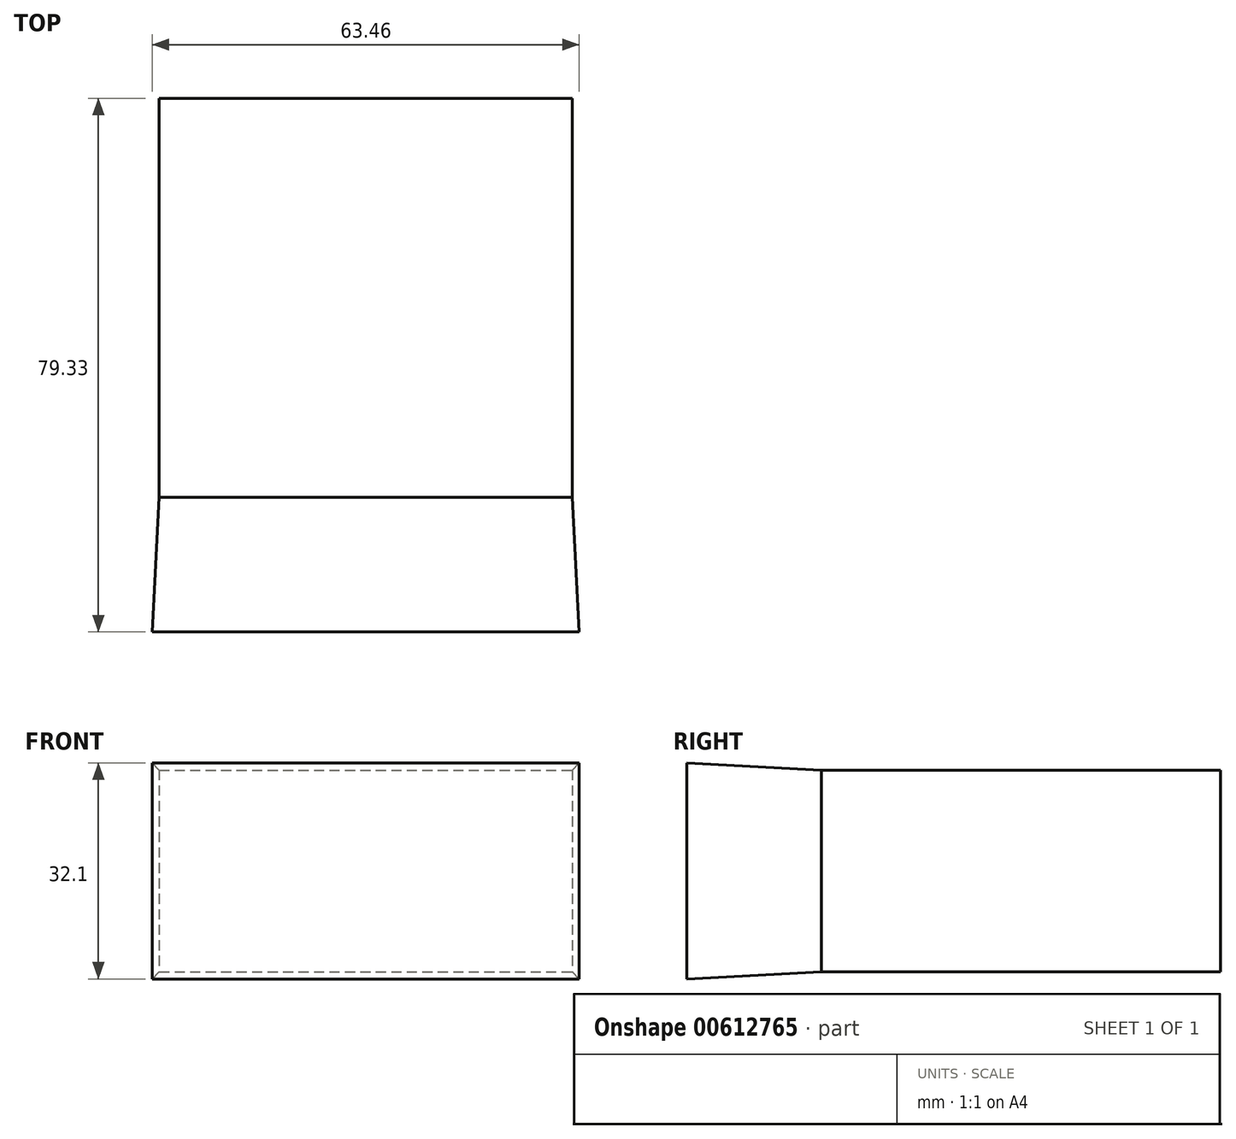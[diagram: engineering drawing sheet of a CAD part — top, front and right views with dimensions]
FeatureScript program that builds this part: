
annotation { "Feature Type Name" : "Feature", "Feature Type Description" : "" }
export const myFeature = defineFeature(function(context is Context, id is Id, definition is map)
    precondition{}
    {
        {
            var Q0;
            Q0=qCreatedBy(makeId("Top.planeOp"),FACE);
            var sketch = newSketch(context, id + "F0", { "sketchPlane" : qUnion([Q0])});
            skLineSegment(sketch, "E0.bottom", {"start": v(-69.42, 20.43) * mm, "end": v(-8.05, 20.43) * mm});
            skLineSegment(sketch, "E0.top", {"start": v(-69.42, -38.9) * mm, "end": v(-8.05, -38.9) * mm});
            skLineSegment(sketch, "E0.left", {"start": v(-69.42, 20.43) * mm, "end": v(-69.42, -38.9) * mm});
            skLineSegment(sketch, "E0.right", {"start": v(-8.05, 20.43) * mm, "end": v(-8.05, -38.9) * mm});
            skSolve(sketch);
        }
        {
            var Q0;
            Q0=makeQuery(id+"F0.imprint","IMPRINT",FACE,{"disambiguationData":[TD([[makeQuery(id+"F0.imprint","IMPRINT",EDGE,{"derivedFrom":sQuery(id+"F0.wireOp",EDGE,"E0.bottom")}),-1.0]])]});
            extrude(context, id + "F1", {"entities" : qUnion([Q0]), "depth" : 30 * mm, "offsetDistance" : 25 * mm});
        }
        {
            var Q0;
            Q0=makeQuery(id+"F1.opExtrude","SWEPT_FACE",FACE,{"disambiguationData":[OSD([sQuery(id+"F0.wireOp",EDGE,"E0.top")])]});
            extrude(context, id + "F2", {"entities" : qUnion([Q0]), "operationType" : NewBodyOperationType.ADD, "depth" : 20 * mm, "offsetDistance" : 25 * mm, "hasDraft" : true, "draftAngle" : 3 * degree});
        }
    });
